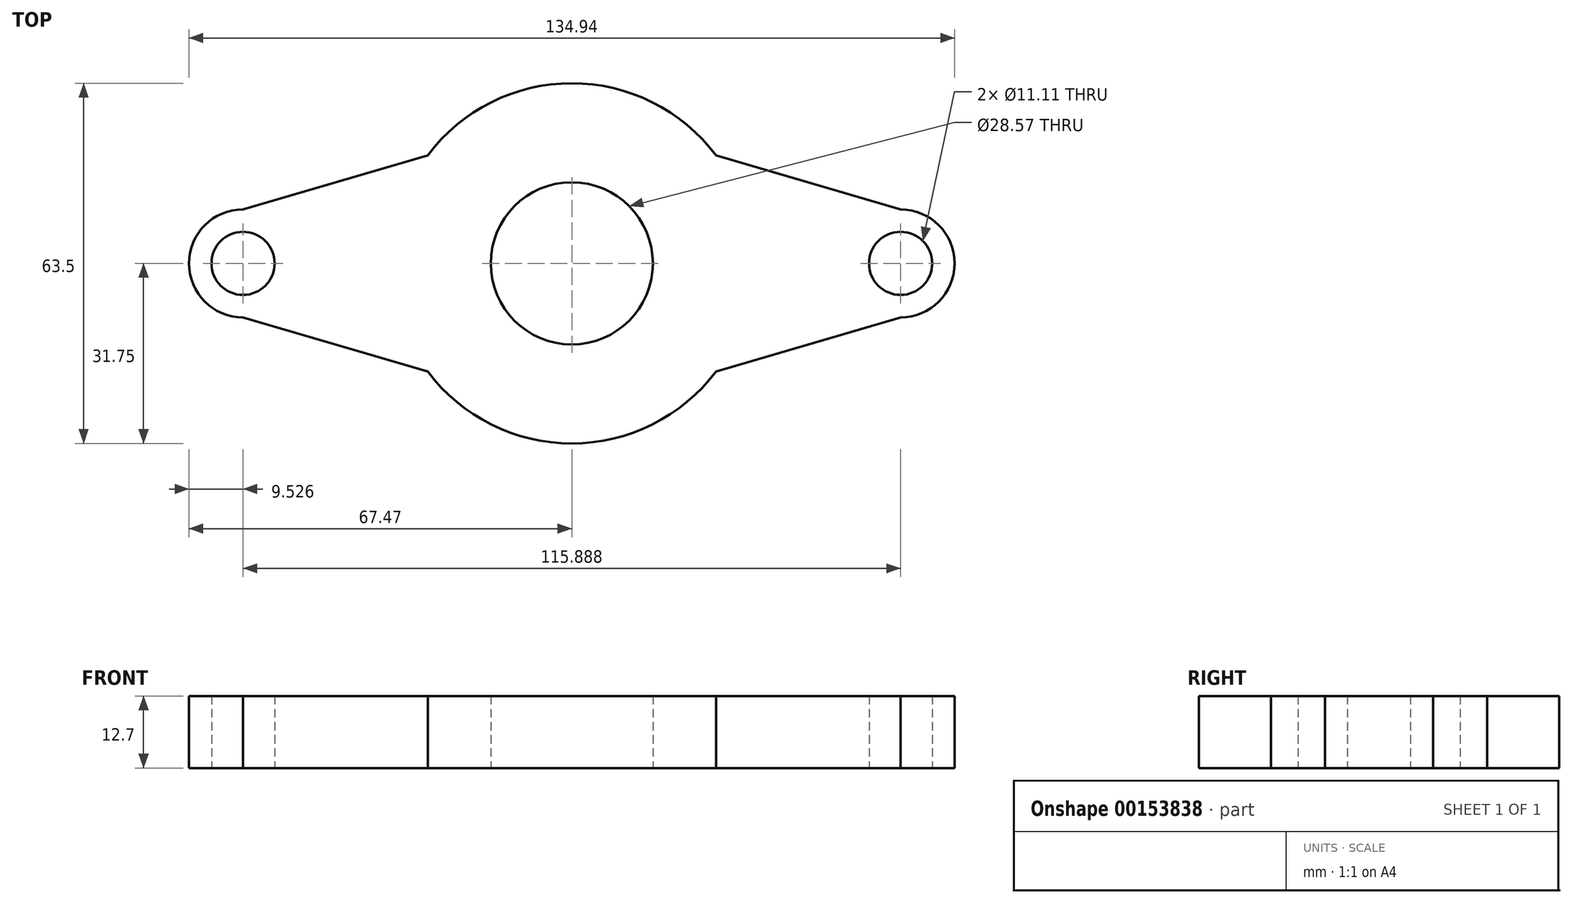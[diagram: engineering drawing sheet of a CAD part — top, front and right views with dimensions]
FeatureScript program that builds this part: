
annotation { "Feature Type Name" : "Feature", "Feature Type Description" : "" }
export const myFeature = defineFeature(function(context is Context, id is Id, definition is map)
    precondition{}
    {
        {
            var Q0;
            Q0=qCreatedBy(makeId("Top.planeOp"),FACE);
            var sketch = newSketch(context, id + "F0", { "sketchPlane" : qUnion([Q0])});
            skCircle(sketch, "E0", {"center": v(0, 0) * mm, "radius": 14.29 * mm});
            skCircle(sketch, "E1", {"center": v(57.94, 0) * mm, "radius": 5.56 * mm});
            skCircle(sketch, "E2.1.0", {"center": v(-57.94, 0) * mm, "radius": 5.56 * mm});
            skLineSegment(sketch, "E3", {"start": v(-57.94, 0) * mm, "end": v(57.94, 0) * mm, "construction": true});
            skCircle(sketch, "E4", {"center": v(0, 0) * mm, "radius": 31.75 * mm});
            skLineSegment(sketch, "E5", {"start": v(-25.4, 19.05) * mm, "end": v(-57.94, 9.53) * mm});
            skLineSegment(sketch, "E6", {"start": v(-25.4, -19.05) * mm, "end": v(-57.94, -9.52) * mm});
            skLineSegment(sketch, "E7", {"start": v(25.4, 19.05) * mm, "end": v(57.94, 9.53) * mm});
            skLineSegment(sketch, "E8", {"start": v(25.4, -19.05) * mm, "end": v(57.94, -9.52) * mm});
            skArc(sketch, "E9", {"start": v(-57.94, 9.53) * mm, "mid": v(-67.47, 0) * mm, "end": v(-57.94, -9.53) * mm});
            skArc(sketch, "E10", {"start": v(57.94, -9.53) * mm, "mid": v(67.47, 0) * mm, "end": v(57.94, 9.53) * mm});
            skLineSegment(sketch, "E11", {"start": v(-25.4, 41.67) * mm, "end": v(-25.4, -47.6) * mm, "construction": true});
            skLineSegment(sketch, "E12", {"start": v(25.4, 41.51) * mm, "end": v(25.4, -47.13) * mm, "construction": true});
            skLineSegment(sketch, "E13", {"start": v(-57.94, -31.24) * mm, "end": v(-57.94, 29.83) * mm, "construction": true});
            skLineSegment(sketch, "E14", {"start": v(57.94, -37) * mm, "end": v(57.94, 29.83) * mm, "construction": true});
            skSolve(sketch);
        }
        {
            var Q0;
            Q0=makeQuery(id+"F0.imprint","IMPRINT",FACE,{"disambiguationData":[TD([[makeQuery(id+"F0.imprint","IMPRINT",EDGE,{"derivedFrom":sQuery(id+"F0.wireOp",EDGE,"E0")}),-1.0]])]});
            var Q1;
            Q1=makeQuery(id+"F0.imprint","IMPRINT",FACE,{"disambiguationData":[TD([[makeQuery(id+"F0.imprint","IMPRINT",EDGE,{"derivedFrom":sQuery(id+"F0.wireOp",EDGE,"E2.1.0")}),-1.0]])]});
            var Q2;
            Q2=makeQuery(id+"F0.imprint","IMPRINT",FACE,{"disambiguationData":[TD([[makeQuery(id+"F0.imprint","IMPRINT",EDGE,{"derivedFrom":sQuery(id+"F0.wireOp",EDGE,"E1")}),-1.0]])]});
            extrude(context, id + "F1", {"entities" : qUnion([Q0, Q1, Q2]), "depth" : 12.7 * mm});
        }
    });
